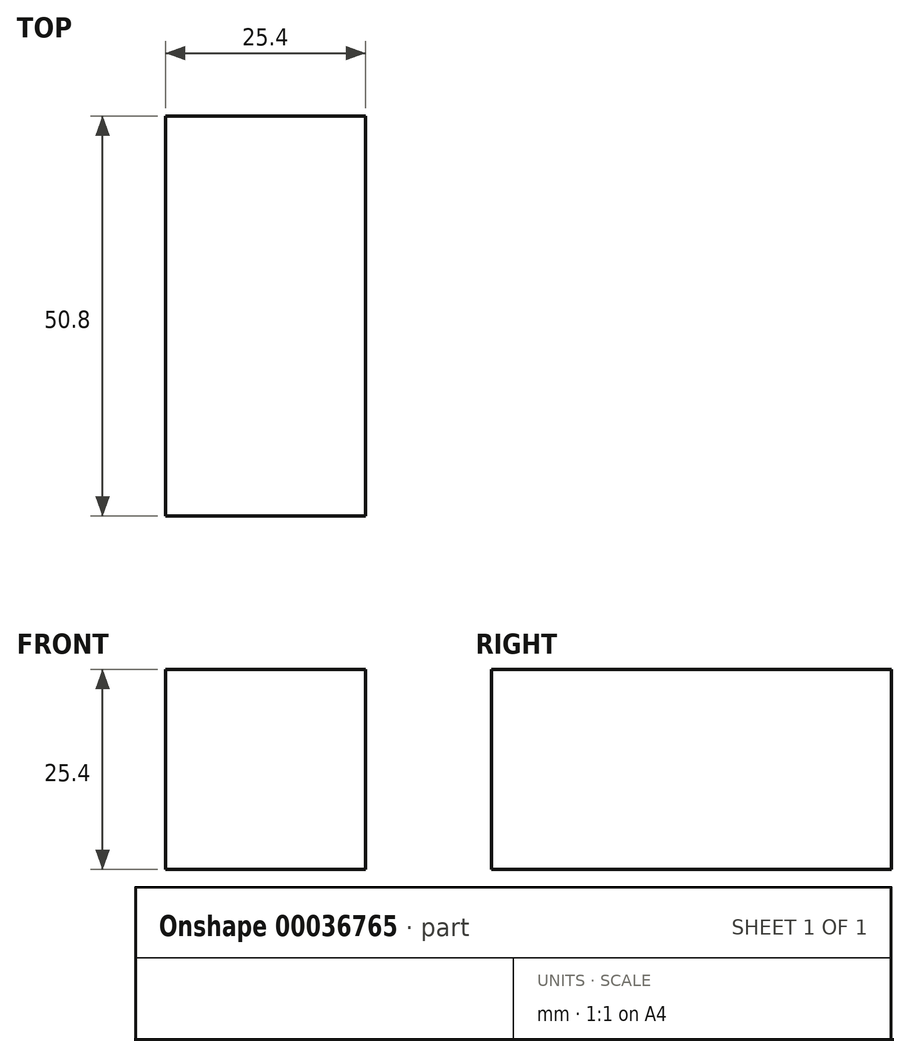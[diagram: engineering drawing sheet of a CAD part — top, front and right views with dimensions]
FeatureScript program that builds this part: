
annotation { "Feature Type Name" : "Feature", "Feature Type Description" : "" }
export const myFeature = defineFeature(function(context is Context, id is Id, definition is map)
    precondition{}
    {
        {
            var Q0;
            Q0=qCreatedBy(makeId("Front.planeOp"),FACE);
            var sketch = newSketch(context, id + "F0", { "sketchPlane" : qUnion([Q0])});
            skLineSegment(sketch, "E0.bottom", {"start": v(0, 0) * mm, "end": v(25.4, 0) * mm});
            skLineSegment(sketch, "E0.top", {"start": v(0, -25.4) * mm, "end": v(25.4, -25.4) * mm});
            skLineSegment(sketch, "E0.left", {"start": v(0, 0) * mm, "end": v(0, -25.4) * mm});
            skLineSegment(sketch, "E0.right", {"start": v(25.4, 0) * mm, "end": v(25.4, -25.4) * mm});
            skSolve(sketch);
        }
        {
            var Q0;
            Q0=makeQuery(id+"F0.imprint","IMPRINT",FACE,{"disambiguationData":[TD([[makeQuery(id+"F0.imprint","IMPRINT",EDGE,{"derivedFrom":sQuery(id+"F0.wireOp",EDGE,"E0.bottom")}),-1.0]])]});
            extrude(context, id + "F1", {"entities" : qUnion([Q0]), "depth" : 50.8 * mm});
        }
    });
